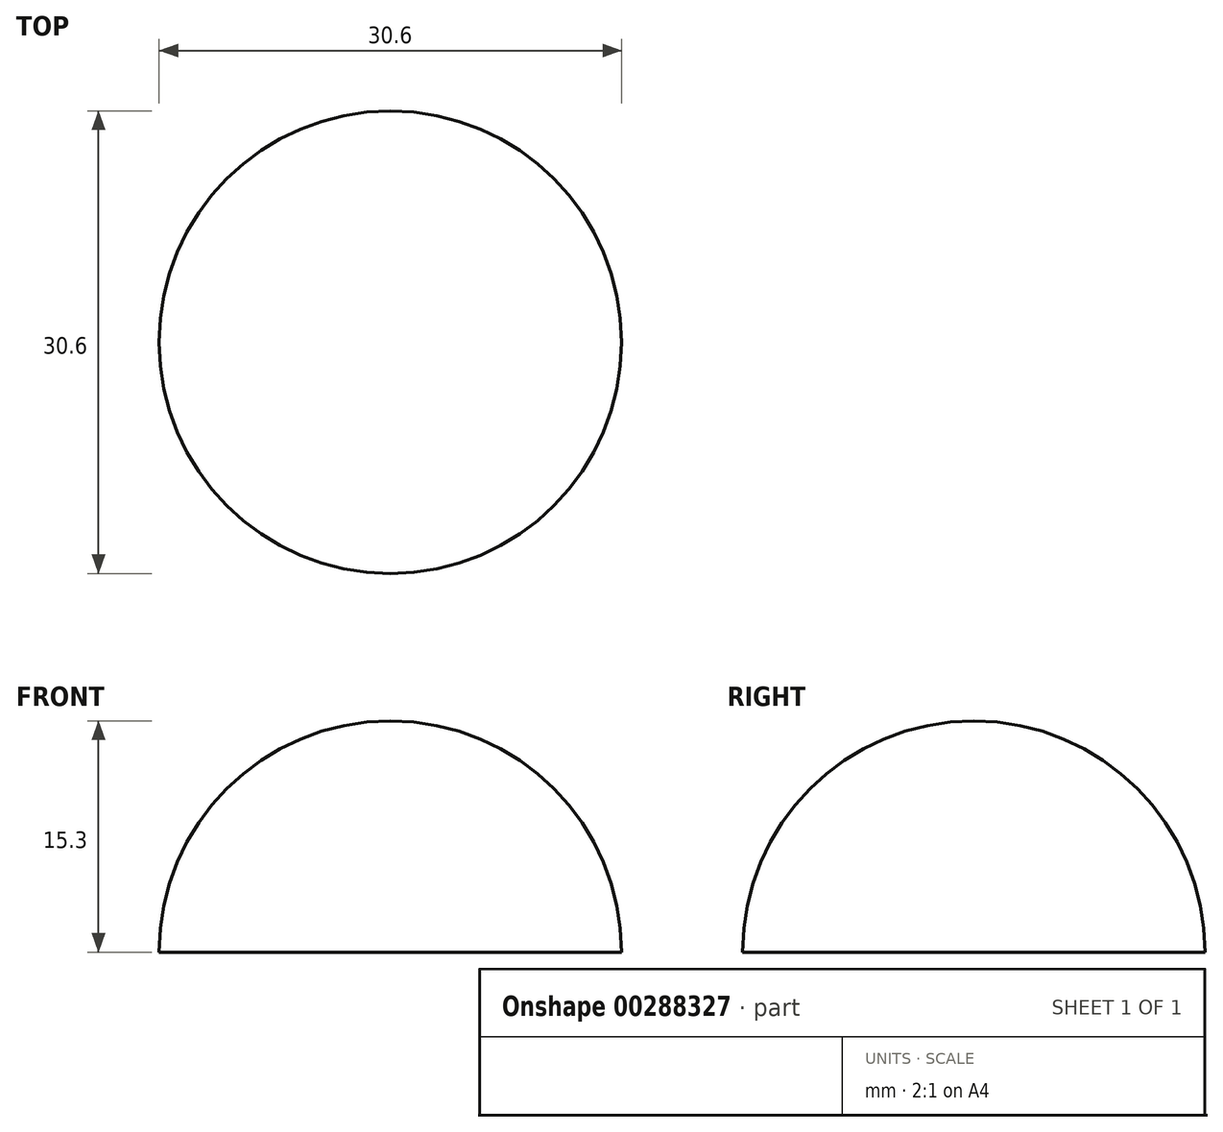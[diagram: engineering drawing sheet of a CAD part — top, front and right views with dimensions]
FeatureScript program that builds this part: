
annotation { "Feature Type Name" : "Feature", "Feature Type Description" : "" }
export const myFeature = defineFeature(function(context is Context, id is Id, definition is map)
    precondition{}
    {
        {
            var Q0;
            Q0=qCreatedBy(makeId("Top.planeOp"),FACE);
            var sketch = newSketch(context, id + "F0", { "sketchPlane" : qUnion([Q0])});
            skArc(sketch, "E0", {"start": v(-15.3, 0) * mm, "mid": v(0, -15.3) * mm, "end": v(15.3, 0) * mm});
            skLineSegment(sketch, "E1", {"start": v(-15.3, 0) * mm, "end": v(15.3, 0) * mm});
            skSolve(sketch);
        }
        {
            var Q0;
            Q0=makeQuery(id+"F0.imprint","IMPRINT",FACE,{"disambiguationData":[TD([[makeQuery(id+"F0.imprint","IMPRINT",EDGE,{"derivedFrom":sQuery(id+"F0.wireOp",EDGE,"E0")}),1.0]])]});
            var Q1;
            Q1=sQuery(id+"F0.wireOp",EDGE,"E1");
            revolve(context, id + "F1", {"entities" : qUnion([Q0]), "axis" : qUnion([Q1]), "revolveType" : RevolveType.ONE_DIRECTION, "oppositeDirection" : true, "angle" : 180 * degree});
        }
    });
